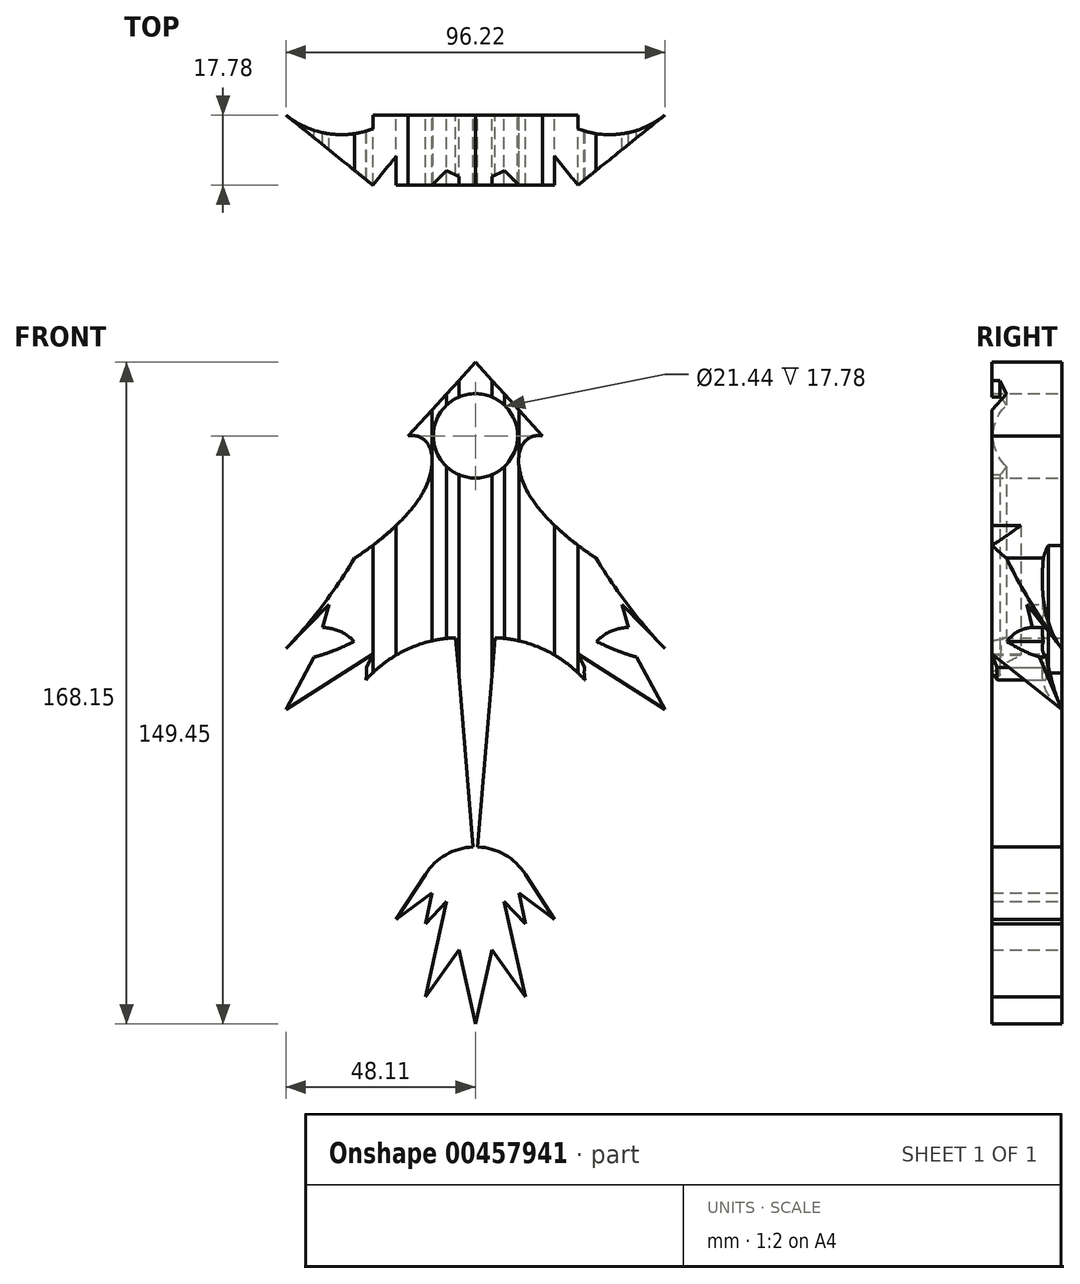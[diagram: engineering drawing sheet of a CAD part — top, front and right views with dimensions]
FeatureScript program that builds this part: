
annotation { "Feature Type Name" : "Feature", "Feature Type Description" : "" }
export const myFeature = defineFeature(function(context is Context, id is Id, definition is map)
    precondition{}
    {
        {
            var Q0;
            Q0=qCreatedBy(makeId("Front.planeOp"),FACE);
            var sketch = newSketch(context, id + "F0", { "sketchPlane" : qUnion([Q0])});
            skCircle(sketch, "E0", {"center": v(0, 0) * mm, "radius": 10.72 * mm});
            skArc(sketch, "E1", {"start": v(17.07, 0) * mm, "mid": v(0, 18.7) * mm, "end": v(-17.07, 0) * mm});
            skPoint(sketch, "E2", {"position": v(0, 18.7) * mm});
            skLineSegment(sketch, "E3", {"start": v(-17.07, 0) * mm, "end": v(0, 18.7) * mm});
            skLineSegment(sketch, "E4", {"start": v(17.07, 0) * mm, "end": v(0, 18.7) * mm});
            skFitSpline(sketch, "E5", {"points": [v(-17.07, 0) * mm, v(-49.18, -36.6) * mm, v(-13.33, -14.4) * mm, v(-17.07, 0) * mm]});
            skFitSpline(sketch, "E6", {"points": [v(-13.33, -14.4) * mm, v(-49.4, -55.37) * mm, v(-5.01, -30.4) * mm, v(-13.33, -14.4) * mm]});
            skFitSpline(sketch, "E7", {"points": [v(-5.01, -30.4) * mm, v(-48.11, -69.56) * mm, v(-5.01, -51.3) * mm, v(-5.01, -30.4) * mm]});
            skFitSpline(sketch, "E8.MirrorC", {"points": [v(17.07, 0) * mm, v(49.18, -36.6) * mm, v(13.33, -14.4) * mm, v(17.07, 0) * mm]});
            skFitSpline(sketch, "E9.MirrorC", {"points": [v(13.33, -14.4) * mm, v(49.4, -55.37) * mm, v(5.01, -30.4) * mm, v(13.33, -14.4) * mm]});
            skFitSpline(sketch, "E10.MirrorC", {"points": [v(5.01, -30.4) * mm, v(48.11, -69.56) * mm, v(5.01, -51.3) * mm, v(5.01, -30.4) * mm]});
            skLineSegment(sketch, "E11", {"start": v(-5.01, -51.3) * mm, "end": v(0, -111.38) * mm});
            skLineSegment(sketch, "E12", {"start": v(0, -111.38) * mm, "end": v(5.01, -51.3) * mm});
            skArc(sketch, "E13", {"start": v(12.7, -111.38) * mm, "mid": v(0, -104.45) * mm, "end": v(-12.7, -111.38) * mm});
            skLineSegment(sketch, "E14", {"start": v(-12.7, -111.38) * mm, "end": v(-20.1, -122.89) * mm});
            skLineSegment(sketch, "E15", {"start": v(-20.1, -122.89) * mm, "end": v(-11.07, -116.15) * mm});
            skLineSegment(sketch, "E16", {"start": v(-11.07, -116.15) * mm, "end": v(-12.7, -124) * mm});
            skLineSegment(sketch, "E17", {"start": v(-12.7, -124) * mm, "end": v(-7.31, -118.28) * mm});
            skLineSegment(sketch, "E18.MirrorCS", {"start": v(12.7, -124) * mm, "end": v(7.31, -118.28) * mm});
            skLineSegment(sketch, "E19.MirrorCS", {"start": v(11.07, -116.15) * mm, "end": v(12.7, -124) * mm});
            skLineSegment(sketch, "E20.MirrorCS", {"start": v(20.1, -122.89) * mm, "end": v(11.07, -116.15) * mm});
            skLineSegment(sketch, "E21.MirrorCS", {"start": v(12.7, -111.38) * mm, "end": v(20.1, -122.89) * mm});
            skLineSegment(sketch, "E22", {"start": v(-17.07, 0) * mm, "end": v(-49.18, -36.6) * mm});
            skLineSegment(sketch, "E23", {"start": v(-41.28, -36.6) * mm, "end": v(-49.4, -55.37) * mm});
            skLineSegment(sketch, "E24", {"start": v(-40.98, -56.2) * mm, "end": v(-48.11, -69.56) * mm});
            skLineSegment(sketch, "E25", {"start": v(-48.11, -69.56) * mm, "end": v(-26.05, -55.37) * mm});
            skLineSegment(sketch, "E26", {"start": v(-26.05, -55.37) * mm, "end": v(-32.77, -69.56) * mm});
            skLineSegment(sketch, "E27", {"start": v(-32.77, -69.56) * mm, "end": v(-5.01, -51.3) * mm});
            skLineSegment(sketch, "E28", {"start": v(-41.28, -36.6) * mm, "end": v(-49.18, -36.6) * mm});
            skLineSegment(sketch, "E29", {"start": v(-40.98, -56.2) * mm, "end": v(-49.4, -55.37) * mm});
            skLineSegment(sketch, "E30", {"start": v(-49.4, -55.37) * mm, "end": v(-37.18, -42.84) * mm});
            skLineSegment(sketch, "E31", {"start": v(-37.18, -42.84) * mm, "end": v(-40.98, -56.2) * mm});
            skLineSegment(sketch, "E32", {"start": v(-7.31, -118.28) * mm, "end": v(-12.7, -142.6) * mm});
            skLineSegment(sketch, "E33", {"start": v(-12.7, -142.6) * mm, "end": v(-4.21, -130.6) * mm});
            skLineSegment(sketch, "E34", {"start": v(-4.21, -130.6) * mm, "end": v(0, -149.45) * mm});
            skLineSegment(sketch, "E35.MirrorCS", {"start": v(4.21, -130.6) * mm, "end": v(0, -149.45) * mm});
            skLineSegment(sketch, "E36.MirrorCS", {"start": v(12.7, -142.6) * mm, "end": v(4.21, -130.6) * mm});
            skLineSegment(sketch, "E37.MirrorCS", {"start": v(7.31, -118.28) * mm, "end": v(12.7, -142.6) * mm});
            skLineSegment(sketch, "E38.MirrorCS", {"start": v(17.07, 0) * mm, "end": v(49.18, -36.6) * mm});
            skLineSegment(sketch, "E39.MirrorCS", {"start": v(41.28, -36.6) * mm, "end": v(49.18, -36.6) * mm});
            skLineSegment(sketch, "E40.MirrorCS", {"start": v(41.28, -36.6) * mm, "end": v(49.4, -55.37) * mm});
            skLineSegment(sketch, "E41.MirrorCS", {"start": v(49.4, -55.37) * mm, "end": v(37.18, -42.84) * mm});
            skLineSegment(sketch, "E42.MirrorCS", {"start": v(37.18, -42.84) * mm, "end": v(40.98, -56.2) * mm});
            skLineSegment(sketch, "E43.MirrorCS", {"start": v(40.98, -56.2) * mm, "end": v(48.11, -69.56) * mm});
            skLineSegment(sketch, "E44.MirrorCS", {"start": v(48.11, -69.56) * mm, "end": v(26.05, -55.37) * mm});
            skLineSegment(sketch, "E45.MirrorCS", {"start": v(26.05, -55.37) * mm, "end": v(32.77, -69.56) * mm});
            skLineSegment(sketch, "E46.MirrorCS", {"start": v(32.77, -69.56) * mm, "end": v(5.01, -51.3) * mm});
            skArc(sketch, "E47", {"start": v(-49.4, -55.37) * mm, "mid": v(-29.84, -29.67) * mm, "end": v(-17.07, 0) * mm});
            skArc(sketch, "E48.MirrorCS", {"start": v(49.4, -55.37) * mm, "mid": v(29.84, -29.67) * mm, "end": v(17.07, 0) * mm});
            skArc(sketch, "E49", {"start": v(-32.77, -69.56) * mm, "mid": v(-31.64, -51.4) * mm, "end": v(-49.4, -55.37) * mm});
            skArc(sketch, "E50.MirrorCS", {"start": v(32.77, -69.56) * mm, "mid": v(31.64, -51.4) * mm, "end": v(49.4, -55.37) * mm});
            skArc(sketch, "E51", {"start": v(-5.01, -51.3) * mm, "mid": v(-21.45, -56.54) * mm, "end": v(-32.77, -69.56) * mm});
            skArc(sketch, "E52.MirrorCS", {"start": v(5.01, -51.3) * mm, "mid": v(21.45, -56.54) * mm, "end": v(32.77, -69.56) * mm});
            skSolve(sketch);
        }
        {
            var Q0;
            Q0=makeQuery(id+"F0.imprint","IMPRINT",FACE,{"disambiguationData":[TD([[makeQuery(id+"F0.imprint","IMPRINT",EDGE,{"derivedFrom":sQuery(id+"F0.wireOp",EDGE,"E0")}),-1.0]])]});
            var Q1;
            {var subQ10=sQuery(id+"F0.wireOp",EDGE,"E30");Q1=makeQuery(id+"F0.imprint","IMPRINT",FACE,{"disambiguationData":[TD([[makeQuery(id+"F0.imprint","IMPRINT",EDGE,{"derivedFrom":subQ10}),1.0]])]});}
            var Q2;
            {var subQ5=sQuery(id+"F0.wireOp",EDGE,"E41.MirrorCS");Q2=makeQuery(id+"F0.imprint","IMPRINT",FACE,{"disambiguationData":[TD([[makeQuery(id+"F0.imprint","IMPRINT",EDGE,{"derivedFrom":subQ5}),-1.0]])]});}
            var Q3;
            {var subQ0=sQuery(id+"F0.wireOp",EDGE,"E7");var subQ1=sQuery(id+"F0.wireOp",EDGE,"E6");var subQ3=makeQuery(id+"F0.imprint","INTERSECT",VERTEX,{"derivedFrom":[subQ1,subQ0]});Q3=makeQuery(id+"F0.imprint","IMPRINT",FACE,{"disambiguationData":[TD([[makeQuery(id+"F0.imprint","IMPRINT",EDGE,{"disambiguationData":[TD([[subQ3,1.0]])],"derivedFrom":subQ1}),1.0]])]});}
            var Q4;
            {var subQ7=sQuery(id+"F0.wireOp",EDGE,"E24");Q4=makeQuery(id+"F0.imprint","IMPRINT",FACE,{"disambiguationData":[TD([[makeQuery(id+"F0.imprint","IMPRINT",EDGE,{"derivedFrom":subQ7}),1.0]])]});}
            var Q5;
            {var subQ0=sQuery(id+"F0.wireOp",EDGE,"E10.MirrorC");var subQ1=sQuery(id+"F0.wireOp",EDGE,"E9.MirrorC");var subQ3=makeQuery(id+"F0.imprint","INTERSECT",VERTEX,{"derivedFrom":[subQ1,subQ0]});Q5=makeQuery(id+"F0.imprint","IMPRINT",FACE,{"disambiguationData":[TD([[makeQuery(id+"F0.imprint","IMPRINT",EDGE,{"disambiguationData":[TD([[subQ3,1.0]])],"derivedFrom":subQ1}),-1.0]])]});}
            var Q6;
            {var subQ7=sQuery(id+"F0.wireOp",EDGE,"E43.MirrorCS");Q6=makeQuery(id+"F0.imprint","IMPRINT",FACE,{"disambiguationData":[TD([[makeQuery(id+"F0.imprint","IMPRINT",EDGE,{"derivedFrom":subQ7}),-1.0]])]});}
            var Q7;
            {var subQ3=sQuery(id+"F0.wireOp",EDGE,"E13");var subQ5=sQuery(id+"F0.wireOp",EDGE,"E11");var subQ8=makeQuery(id+"F0.imprint","INTERSECT",VERTEX,{"derivedFrom":[subQ5,subQ3]});Q7=makeQuery(id+"F0.imprint","IMPRINT",FACE,{"disambiguationData":[TD([[makeQuery(id+"F0.imprint","IMPRINT",EDGE,{"disambiguationData":[TD([[subQ8,1.0]])],"derivedFrom":subQ3}),-1.0]])]});}
            var Q8;
            {var subQ6=sQuery(id+"F0.wireOp",EDGE,"E8.MirrorC");var subQ11=sQuery(id+"F0.wireOp",EDGE,"E48.MirrorCS");var subQ12=makeQuery(id+"F0.imprint","INTERSECT",VERTEX,{"derivedFrom":[subQ6,subQ11]});Q8=makeQuery(id+"F0.imprint","IMPRINT",FACE,{"disambiguationData":[TD([[makeQuery(id+"F0.imprint","IMPRINT",EDGE,{"disambiguationData":[TD([[subQ12,-1.0]])],"derivedFrom":subQ6}),1.0]])]});}
            var Q9;
            {var subQ6=sQuery(id+"F0.wireOp",EDGE,"E5");var subQ11=sQuery(id+"F0.wireOp",EDGE,"E47");var subQ12=makeQuery(id+"F0.imprint","INTERSECT",VERTEX,{"derivedFrom":[subQ6,subQ11]});Q9=makeQuery(id+"F0.imprint","IMPRINT",FACE,{"disambiguationData":[TD([[makeQuery(id+"F0.imprint","IMPRINT",EDGE,{"disambiguationData":[TD([[subQ12,-1.0]])],"derivedFrom":subQ6}),-1.0]])]});}
            var Q10;
            {var subQ0=sQuery(id+"F0.wireOp",EDGE,"E10.MirrorC");var subQ1=sQuery(id+"F0.wireOp",EDGE,"E7");var subQ7=makeQuery(id+"F0.imprint","INTERSECT",VERTEX,{"disambiguationData":[OD(0.0)],"derivedFrom":[subQ1,subQ0]});Q10=makeQuery(id+"F0.imprint","IMPRINT",FACE,{"disambiguationData":[TD([[makeQuery(id+"F0.imprint","IMPRINT",EDGE,{"disambiguationData":[TD([[subQ7,-1.0]])],"derivedFrom":subQ1}),-1.0]])]});}
            var Q11;
            {var subQ1=sQuery(id+"F0.wireOp",EDGE,"E6");var subQ8=sQuery(id+"F0.wireOp",EDGE,"E49");var subQ15=makeQuery(id+"F0.imprint","INTERSECT",VERTEX,{"derivedFrom":[subQ1,subQ8]});Q11=makeQuery(id+"F0.imprint","IMPRINT",FACE,{"disambiguationData":[TD([[makeQuery(id+"F0.imprint","IMPRINT",EDGE,{"disambiguationData":[TD([[subQ15,-1.0]])],"derivedFrom":subQ1}),-1.0]])]});}
            var Q12;
            {var subQ0=sQuery(id+"F0.wireOp",EDGE,"E10.MirrorC");var subQ1=sQuery(id+"F0.wireOp",EDGE,"E7");var subQ2=makeQuery(id+"F0.imprint","INTERSECT",VERTEX,{"disambiguationData":[OD(0.0)],"derivedFrom":[subQ1,subQ0]});Q12=makeQuery(id+"F0.imprint","IMPRINT",FACE,{"disambiguationData":[TD([[makeQuery(id+"F0.imprint","IMPRINT",EDGE,{"disambiguationData":[TD([[subQ2,-1.0]])],"derivedFrom":subQ1}),1.0]])]});}
            var Q13;
            {var subQ0=sQuery(id+"F0.wireOp",EDGE,"E14");Q13=makeQuery(id+"F0.imprint","IMPRINT",FACE,{"disambiguationData":[TD([[makeQuery(id+"F0.imprint","IMPRINT",EDGE,{"derivedFrom":subQ0}),1.0]])]});}
            var Q14;
            {var subQ0=sQuery(id+"F0.wireOp",EDGE,"E12");var subQ1=sQuery(id+"F0.wireOp",EDGE,"E11");var subQ2=makeQuery(id+"F0.imprint","INTERSECT",VERTEX,{"derivedFrom":[subQ1,subQ0]});Q14=makeQuery(id+"F0.imprint","IMPRINT",FACE,{"disambiguationData":[TD([[makeQuery(id+"F0.imprint","IMPRINT",EDGE,{"disambiguationData":[TD([[subQ2,1.0]])],"derivedFrom":subQ1}),1.0]])]});}
            extrude(context, id + "F1", {"entities" : qUnion([Q0, Q1, Q2, Q3, Q4, Q5, Q6, Q7, Q8, Q9, Q10, Q11, Q12, Q13, Q14]), "depth" : 17.78 * mm, "offsetDistance" : 25.4 * mm});
        }
        {
            var Q0;
            Q0=makeQuery(id+"F1.opExtrude","SWEPT_FACE",FACE,{"disambiguationData":[OSD([sQuery(id+"F0.wireOp",EDGE,"E52.MirrorCS")])]});
            cPlane(context, id + "F2", {"entities" : qUnion([Q0]), "cplaneType" : CPlaneType.LINE_ANGLE, "offset" : 25.4 * mm, "angle" : 0 * degree, "width" : 152.4 * mm, "height" : 152.4 * mm});
        }
        {
            var Q0;
            Q0=qCreatedBy(id+"F2.planeOp",FACE);
            var sketch = newSketch(context, id + "F3", { "sketchPlane" : qUnion([Q0])});
            skLineSegment(sketch, "E53.0.0", {"start": v(-48.11, 0) * mm, "end": v(-26.05, 0) * mm});
            skLineSegment(sketch, "E53.0.1", {"start": v(-26.05, 0) * mm, "end": v(-26.05, 17.78) * mm});
            skLineSegment(sketch, "E53.0.2", {"start": v(-26.05, 17.78) * mm, "end": v(-48.11, 17.78) * mm});
            skLineSegment(sketch, "E53.0.3", {"start": v(-48.11, 17.78) * mm, "end": v(-48.11, 0) * mm});
            skLineSegment(sketch, "E54.0.0", {"start": v(26.05, 0) * mm, "end": v(48.11, 0) * mm});
            skLineSegment(sketch, "E54.0.1", {"start": v(48.11, 0) * mm, "end": v(48.11, 17.78) * mm});
            skLineSegment(sketch, "E54.0.2", {"start": v(48.11, 17.78) * mm, "end": v(26.05, 17.78) * mm});
            skLineSegment(sketch, "E54.0.3", {"start": v(26.05, 17.78) * mm, "end": v(26.05, 0) * mm});
            skLineSegment(sketch, "E55.0.0", {"start": v(-12.7, 0) * mm, "end": v(-4.21, 0) * mm});
            skLineSegment(sketch, "E55.0.1", {"start": v(-4.21, 0) * mm, "end": v(-4.21, 17.78) * mm});
            skLineSegment(sketch, "E55.0.2", {"start": v(-4.21, 17.78) * mm, "end": v(-12.7, 17.78) * mm});
            skLineSegment(sketch, "E55.0.3", {"start": v(-12.7, 17.78) * mm, "end": v(-12.7, 0) * mm});
            skLineSegment(sketch, "E56.0.0", {"start": v(4.21, 0) * mm, "end": v(12.7, 0) * mm});
            skLineSegment(sketch, "E56.0.1", {"start": v(12.7, 0) * mm, "end": v(12.7, 17.78) * mm});
            skLineSegment(sketch, "E56.0.2", {"start": v(12.7, 17.78) * mm, "end": v(4.21, 17.78) * mm});
            skLineSegment(sketch, "E56.0.3", {"start": v(4.21, 17.78) * mm, "end": v(4.21, 0) * mm});
            skLineSegment(sketch, "E57.0.0", {"start": v(-20.1, 0) * mm, "end": v(-11.07, 0) * mm});
            skLineSegment(sketch, "E57.0.1", {"start": v(-11.07, 0) * mm, "end": v(-11.07, 17.78) * mm});
            skLineSegment(sketch, "E57.0.2", {"start": v(-11.07, 17.78) * mm, "end": v(-20.1, 17.78) * mm});
            skLineSegment(sketch, "E57.0.3", {"start": v(-20.1, 17.78) * mm, "end": v(-20.1, 0) * mm});
            skLineSegment(sketch, "E58.0.0", {"start": v(11.07, 0) * mm, "end": v(20.1, 0) * mm});
            skLineSegment(sketch, "E58.0.1", {"start": v(20.1, 0) * mm, "end": v(20.1, 17.78) * mm});
            skLineSegment(sketch, "E58.0.2", {"start": v(20.1, 17.78) * mm, "end": v(11.07, 17.78) * mm});
            skLineSegment(sketch, "E58.0.3", {"start": v(11.07, 17.78) * mm, "end": v(11.07, 0) * mm});
            skLineSegment(sketch, "E59", {"start": v(-48.11, 0) * mm, "end": v(-26.05, 17.78) * mm});
            skLineSegment(sketch, "E60", {"start": v(48.11, 0) * mm, "end": v(26.05, 17.78) * mm});
            skLineSegment(sketch, "E61", {"start": v(26.05, 17.78) * mm, "end": v(20.1, 10.4) * mm});
            skLineSegment(sketch, "E62", {"start": v(20.1, 10.4) * mm, "end": v(12.7, 17.78) * mm});
            skLineSegment(sketch, "E63", {"start": v(12.7, 17.78) * mm, "end": v(8.46, 13.53) * mm});
            skPoint(sketch, "E63.endSnap0", {"position": v(8.46, 17.78) * mm});
            skLineSegment(sketch, "E64", {"start": v(8.46, 13.53) * mm, "end": v(0, 17.78) * mm});
            skLineSegment(sketch, "E65.MirrorCS", {"start": v(-26.05, 17.78) * mm, "end": v(-20.1, 10.4) * mm});
            skLineSegment(sketch, "E66.MirrorCS", {"start": v(-20.1, 10.4) * mm, "end": v(-12.7, 17.78) * mm});
            skLineSegment(sketch, "E67.MirrorCS", {"start": v(-8.46, 13.53) * mm, "end": v(0, 17.78) * mm});
            skLineSegment(sketch, "E68.MirrorCS", {"start": v(-12.7, 17.78) * mm, "end": v(-8.46, 13.53) * mm});
            skLineSegment(sketch, "E69", {"start": v(-48.11, 17.78) * mm, "end": v(48.11, 17.78) * mm});
            skLineSegment(sketch, "E70", {"start": v(48.11, 17.78) * mm, "end": v(41.75, 5.13) * mm});
            skLineSegment(sketch, "E71", {"start": v(41.75, 5.13) * mm, "end": v(54.52, 17.78) * mm});
            skLineSegment(sketch, "E72", {"start": v(54.52, 17.78) * mm, "end": v(48.11, 17.78) * mm});
            skLineSegment(sketch, "E73", {"start": v(54.52, 17.78) * mm, "end": v(54.52, 0) * mm});
            skLineSegment(sketch, "E74", {"start": v(54.52, 0) * mm, "end": v(48.11, 0) * mm});
            skLineSegment(sketch, "E75.MirrorCS", {"start": v(-54.52, 17.78) * mm, "end": v(-54.52, 0) * mm});
            skLineSegment(sketch, "E76.MirrorCS", {"start": v(-54.52, 17.78) * mm, "end": v(-48.11, 17.78) * mm});
            skLineSegment(sketch, "E77.MirrorCS", {"start": v(-54.52, 0) * mm, "end": v(-48.11, 0) * mm});
            skPoint(sketch, "E78.0", {"position": v(7.31, 17.78) * mm});
            skLineSegment(sketch, "E79.0.0", {"start": v(-4.21, 0) * mm, "end": v(0, 0) * mm});
            skLineSegment(sketch, "E79.0.1", {"start": v(0, 0) * mm, "end": v(0, 17.78) * mm});
            skLineSegment(sketch, "E79.0.2", {"start": v(0, 17.78) * mm, "end": v(-4.21, 17.78) * mm});
            skLineSegment(sketch, "E79.0.3", {"start": v(-4.21, 17.78) * mm, "end": v(-4.21, 0) * mm});
            skLineSegment(sketch, "E80.0.0", {"start": v(0, 0) * mm, "end": v(4.21, 0) * mm});
            skLineSegment(sketch, "E80.0.1", {"start": v(4.21, 0) * mm, "end": v(4.21, 17.78) * mm});
            skLineSegment(sketch, "E80.0.2", {"start": v(4.21, 17.78) * mm, "end": v(0, 17.78) * mm});
            skLineSegment(sketch, "E80.0.3", {"start": v(0, 17.78) * mm, "end": v(0, 0) * mm});
            skLineSegment(sketch, "E81", {"start": v(-11.07, 17.78) * mm, "end": v(-4.21, 10.9) * mm});
            skLineSegment(sketch, "E82", {"start": v(-4.21, 10.9) * mm, "end": v(0, 17.78) * mm});
            skLineSegment(sketch, "E83.MirrorCS", {"start": v(4.21, 10.9) * mm, "end": v(0, 17.78) * mm});
            skLineSegment(sketch, "E84.MirrorCS", {"start": v(11.07, 17.78) * mm, "end": v(4.21, 10.9) * mm});
            skArc(sketch, "E85", {"start": v(-20.1, 0) * mm, "mid": v(-34.1, 4.94) * mm, "end": v(-48.11, 0) * mm});
            skArc(sketch, "E86", {"start": v(0, 0) * mm, "mid": v(-10.05, 3.9) * mm, "end": v(-20.1, 0) * mm});
            skArc(sketch, "E87.MirrorCS", {"start": v(0, 0) * mm, "mid": v(10.05, 3.9) * mm, "end": v(20.1, 0) * mm});
            skArc(sketch, "E88.MirrorCS", {"start": v(20.1, 0) * mm, "mid": v(34.1, 4.94) * mm, "end": v(48.11, 0) * mm});
            skSolve(sketch);
        }
        {
            var Q0;
            {var subQ0=sQuery(id+"F3.wireOp",EDGE,"E53.0.3");Q0=makeQuery(id+"F3.imprint","IMPRINT",FACE,{"disambiguationData":[TD([[makeQuery(id+"F3.imprint","IMPRINT",EDGE,{"derivedFrom":subQ0}),1.0]])]});}
            var Q1;
            Q1=makeQuery(id+"F3.imprint","IMPRINT",FACE,{"disambiguationData":[TD([[makeQuery(id+"F3.imprint","IMPRINT",EDGE,{"derivedFrom":sQuery(id+"F3.wireOp",EDGE,"E53.0.3")}),-1.0]])]});
            var Q2;
            {var subQ3=sQuery(id+"F3.wireOp",EDGE,"E65.MirrorCS");Q2=makeQuery(id+"F3.imprint","IMPRINT",FACE,{"disambiguationData":[TD([[makeQuery(id+"F3.imprint","IMPRINT",EDGE,{"derivedFrom":subQ3}),1.0]])]});}
            var Q3;
            {var subQ3=sQuery(id+"F3.wireOp",EDGE,"E61");Q3=makeQuery(id+"F3.imprint","IMPRINT",FACE,{"disambiguationData":[TD([[makeQuery(id+"F3.imprint","IMPRINT",EDGE,{"derivedFrom":subQ3}),-1.0]])]});}
            var Q4;
            {var subQ3=sQuery(id+"F3.wireOp",EDGE,"E70");Q4=makeQuery(id+"F3.imprint","IMPRINT",FACE,{"disambiguationData":[TD([[makeQuery(id+"F3.imprint","IMPRINT",EDGE,{"derivedFrom":subQ3}),-1.0]])]});}
            var Q5;
            {var subQ1=sQuery(id+"F3.wireOp",EDGE,"E54.0.1");var subQ3=sQuery(id+"F3.wireOp",EDGE,"E71");var subQ4=makeQuery(id+"F3.imprint","INTERSECT",VERTEX,{"derivedFrom":[subQ1,subQ3]});Q5=makeQuery(id+"F3.imprint","IMPRINT",FACE,{"disambiguationData":[TD([[makeQuery(id+"F3.imprint","IMPRINT",EDGE,{"disambiguationData":[TD([[subQ4,1.0]])],"derivedFrom":subQ3}),-1.0]])]});}
            var Q6;
            {var subQ0=sQuery(id+"F3.wireOp",EDGE,"E72");Q6=makeQuery(id+"F3.imprint","IMPRINT",FACE,{"disambiguationData":[TD([[makeQuery(id+"F3.imprint","IMPRINT",EDGE,{"derivedFrom":subQ0}),1.0]])]});}
            var Q7;
            {var subQ4=sQuery(id+"F3.wireOp",EDGE,"E73");Q7=makeQuery(id+"F3.imprint","IMPRINT",FACE,{"disambiguationData":[TD([[makeQuery(id+"F3.imprint","IMPRINT",EDGE,{"derivedFrom":subQ4}),-1.0]])]});}
            var Q8;
            {var subQ0=sQuery(id+"F3.wireOp",EDGE,"E70");Q8=makeQuery(id+"F3.imprint","IMPRINT",FACE,{"disambiguationData":[TD([[makeQuery(id+"F3.imprint","IMPRINT",EDGE,{"derivedFrom":subQ0}),1.0]])]});}
            var Q9;
            {var subQ0=sQuery(id+"F3.wireOp",EDGE,"E84.MirrorCS");var subQ1=sQuery(id+"F3.wireOp",EDGE,"E64");var subQ2=makeQuery(id+"F3.imprint","INTERSECT",VERTEX,{"derivedFrom":[subQ1,subQ0]});Q9=makeQuery(id+"F3.imprint","IMPRINT",FACE,{"disambiguationData":[TD([[makeQuery(id+"F3.imprint","IMPRINT",EDGE,{"disambiguationData":[TD([[subQ2,-1.0]])],"derivedFrom":subQ1}),-1.0]])]});}
            var Q10;
            {var subQ0=sQuery(id+"F3.wireOp",EDGE,"E81");var subQ1=sQuery(id+"F3.wireOp",EDGE,"E67.MirrorCS");var subQ2=makeQuery(id+"F3.imprint","INTERSECT",VERTEX,{"derivedFrom":[subQ1,subQ0]});Q10=makeQuery(id+"F3.imprint","IMPRINT",FACE,{"disambiguationData":[TD([[makeQuery(id+"F3.imprint","IMPRINT",EDGE,{"disambiguationData":[TD([[subQ2,-1.0]])],"derivedFrom":subQ1}),1.0]])]});}
            var Q11;
            {var subQ0=sQuery(id+"F3.wireOp",EDGE,"E79.0.2");Q11=makeQuery(id+"F3.imprint","IMPRINT",FACE,{"disambiguationData":[TD([[makeQuery(id+"F3.imprint","IMPRINT",EDGE,{"derivedFrom":subQ0}),1.0]])]});}
            var Q12;
            {var subQ0=sQuery(id+"F3.wireOp",EDGE,"E80.0.2");Q12=makeQuery(id+"F3.imprint","IMPRINT",FACE,{"disambiguationData":[TD([[makeQuery(id+"F3.imprint","IMPRINT",EDGE,{"derivedFrom":subQ0}),1.0]])]});}
            var Q13;
            {var subQ0=sQuery(id+"F3.wireOp",EDGE,"E53.0.0");Q13=makeQuery(id+"F3.imprint","IMPRINT",FACE,{"disambiguationData":[TD([[makeQuery(id+"F3.imprint","IMPRINT",EDGE,{"derivedFrom":subQ0}),1.0]])]});}
            var Q14;
            {var subQ0=sQuery(id+"F3.wireOp",EDGE,"E54.0.0");Q14=makeQuery(id+"F3.imprint","IMPRINT",FACE,{"disambiguationData":[TD([[makeQuery(id+"F3.imprint","IMPRINT",EDGE,{"derivedFrom":subQ0}),1.0]])]});}
            extrude(context, id + "F4", {"entities" : qUnion([Q0, Q1, Q2, Q3, Q4, Q5, Q6, Q7, Q8, Q9, Q10, Q11, Q12, Q13, Q14]), "operationType" : NewBodyOperationType.REMOVE, "oppositeDirection" : true, "depth" : 101.6 * mm, "offsetDistance" : 25.4 * mm});
        }
    });
